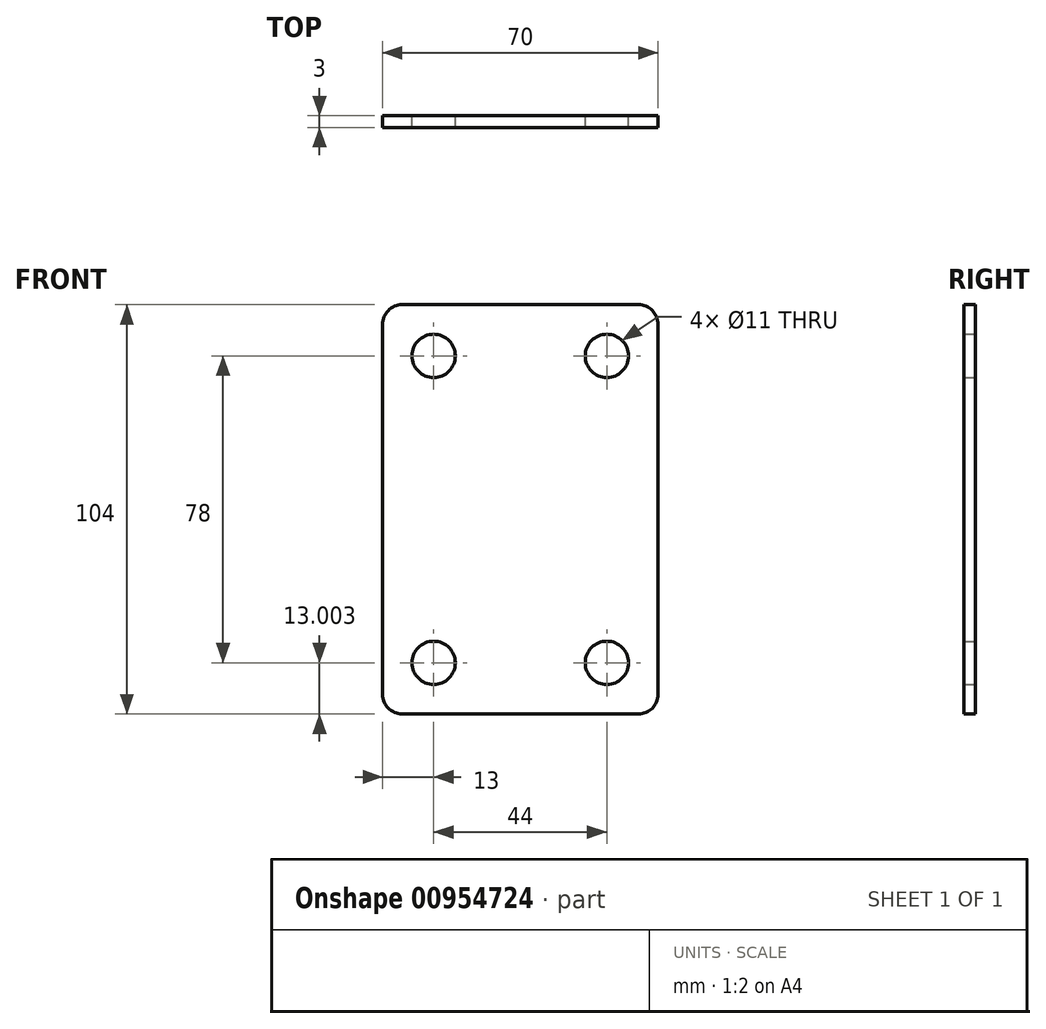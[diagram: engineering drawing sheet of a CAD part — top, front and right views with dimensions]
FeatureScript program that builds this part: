
annotation { "Feature Type Name" : "Feature", "Feature Type Description" : "" }
export const myFeature = defineFeature(function(context is Context, id is Id, definition is map)
    precondition{}
    {
        {
            var Q0;
            Q0=qCreatedBy(makeId("Front.planeOp"),FACE);
            var sketch = newSketch(context, id + "F0", { "sketchPlane" : qUnion([Q0])});
            skLineSegment(sketch, "E0.bottom", {"start": v(5, 73.26) * mm, "end": v(65, 73.26) * mm});
            skLineSegment(sketch, "E0.top", {"start": v(5, -30.74) * mm, "end": v(65, -30.74) * mm});
            skLineSegment(sketch, "E0.left", {"start": v(0, 68.26) * mm, "end": v(0, -25.74) * mm});
            skLineSegment(sketch, "E0.right", {"start": v(70, 68.26) * mm, "end": v(70, -25.74) * mm});
            skPoint(sketch, "E1.visualSharp", {"position": v(0, 73.26) * mm});
            skArc(sketch, "E1.filletArc", {"start": v(5, 73.26) * mm, "mid": v(1.46, 71.8) * mm, "end": v(0, 68.26) * mm});
            skPoint(sketch, "E2.visualSharp", {"position": v(70, 73.26) * mm});
            skArc(sketch, "E2.filletArc", {"start": v(70, 68.26) * mm, "mid": v(68.54, 71.8) * mm, "end": v(65, 73.26) * mm});
            skPoint(sketch, "E3.visualSharp", {"position": v(70, -30.74) * mm});
            skArc(sketch, "E3.filletArc", {"start": v(65, -30.74) * mm, "mid": v(68.54, -29.27) * mm, "end": v(70, -25.74) * mm});
            skPoint(sketch, "E4.visualSharp", {"position": v(0, -30.74) * mm});
            skArc(sketch, "E4.filletArc", {"start": v(0, -25.74) * mm, "mid": v(1.46, -29.27) * mm, "end": v(5, -30.74) * mm});
            skCircle(sketch, "E5", {"center": v(13, 60.26) * mm, "radius": 5.5 * mm});
            skCircle(sketch, "E6", {"center": v(57, 60.26) * mm, "radius": 5.5 * mm});
            skCircle(sketch, "E7", {"center": v(13, -17.74) * mm, "radius": 5.5 * mm});
            skCircle(sketch, "E8", {"center": v(57, -17.74) * mm, "radius": 5.5 * mm});
            skSolve(sketch);
        }
        {
            var Q0;
            Q0=makeQuery(id+"F0.imprint","IMPRINT",FACE,{"disambiguationData":[TD([[makeQuery(id+"F0.imprint","IMPRINT",EDGE,{"derivedFrom":sQuery(id+"F0.wireOp",EDGE,"E0.bottom")}),-1.0]])]});
            extrude(context, id + "F1", {"entities" : qUnion([Q0]), "depth" : 3 * mm, "offsetDistance" : 25 * mm});
        }
    });
